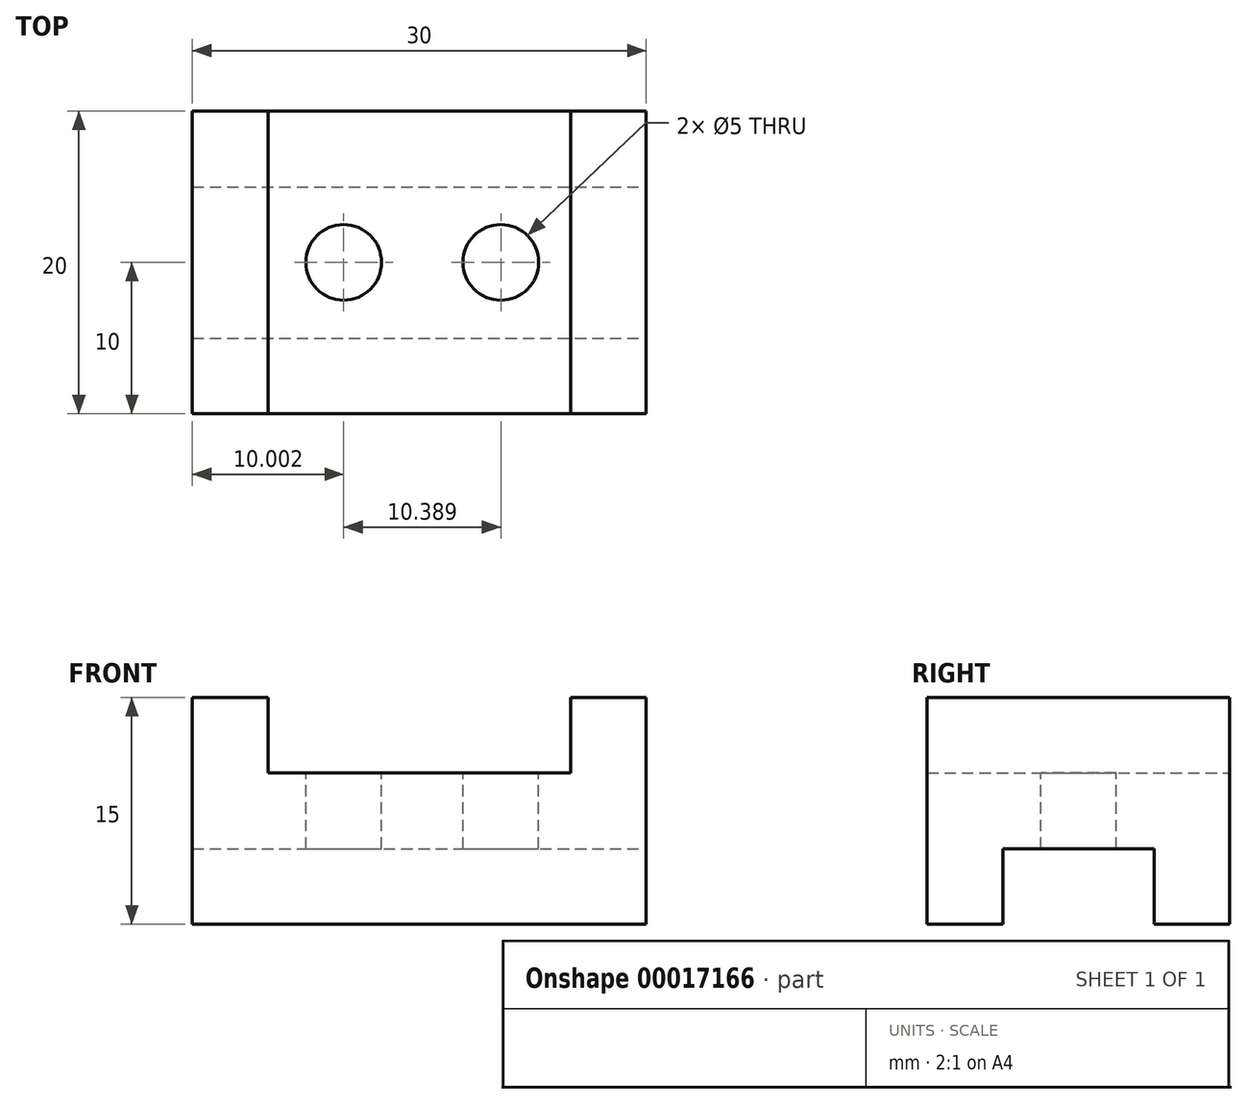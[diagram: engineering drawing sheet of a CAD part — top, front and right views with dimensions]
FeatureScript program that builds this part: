
annotation { "Feature Type Name" : "Feature", "Feature Type Description" : "" }
export const myFeature = defineFeature(function(context is Context, id is Id, definition is map)
    precondition{}
    {
        {
            var Q0;
            Q0=qCreatedBy(makeId("Front.planeOp"),FACE);
            var sketch = newSketch(context, id + "F0", { "sketchPlane" : qUnion([Q0])});
            skLineSegment(sketch, "E0", {"start": v(-25.78, 15) * mm, "end": v(-25.78, 0) * mm});
            skLineSegment(sketch, "E1", {"start": v(-25.78, 0) * mm, "end": v(4.22, 0) * mm});
            skLineSegment(sketch, "E2", {"start": v(4.22, 0) * mm, "end": v(4.22, 15) * mm});
            skLineSegment(sketch, "E3", {"start": v(4.22, 15) * mm, "end": v(-0.78, 15) * mm});
            skLineSegment(sketch, "E4", {"start": v(-0.78, 15) * mm, "end": v(-0.78, 10) * mm});
            skLineSegment(sketch, "E5", {"start": v(-0.78, 10) * mm, "end": v(-20.78, 10) * mm});
            skLineSegment(sketch, "E6", {"start": v(-25.78, 15) * mm, "end": v(-20.78, 15) * mm});
            skLineSegment(sketch, "E7", {"start": v(-20.78, 15) * mm, "end": v(-20.78, 10) * mm});
            skSolve(sketch);
        }
        {
            var Q0;
            Q0 = qSketchRegion(id + "F0", true);
            extrude(context, id + "F1", {"entities" : qUnion([Q0]), "depth" : 20 * mm});
        }
        {
            var Q0;
            Q0=makeQuery(id+"F1.opExtrude","SWEPT_FACE",FACE,{"disambiguationData":[OSD([sQuery(id+"F0.wireOp",EDGE,"E2")])]});
            var sketch = newSketch(context, id + "F2", { "sketchPlane" : qUnion([Q0])});
            skLineSegment(sketch, "E8", {"start": v(-15, 0) * mm, "end": v(-15, 5) * mm});
            skLineSegment(sketch, "E9", {"start": v(-15, 5) * mm, "end": v(-5, 5) * mm});
            skLineSegment(sketch, "E10", {"start": v(-5, 5) * mm, "end": v(-5, 0) * mm});
            skSolve(sketch);
        }
        {
            var Q0;
            Q0 = qSketchRegion(id + "F2", true);
            var Q1;
            {var subQ2=sQuery(id+"F2.wireOp",EDGE,"E8");Q1=makeQuery(id+"F2.imprint","IMPRINT",FACE,{"disambiguationData":[TD([[makeQuery(id+"F2.imprint","IMPRINT",EDGE,{"derivedFrom":subQ2}),-1.0]])]});}
            extrude(context, id + "F3", {"entities" : qUnion([Q0, Q1]), "operationType" : NewBodyOperationType.REMOVE, "endBound" : BoundingType.THROUGH_ALL, "oppositeDirection" : true, "depth" : 25 * mm});
        }
        {
            var Q0;
            Q0=makeQuery(id+"F1.opExtrude","SWEPT_FACE",FACE,{"disambiguationData":[OSD([sQuery(id+"F0.wireOp",EDGE,"E5")])]});
            var sketch = newSketch(context, id + "F4", { "sketchPlane" : qUnion([Q0])});
            skCircle(sketch, "E11", {"center": v(-15.78, -10) * mm, "radius": 2.5 * mm});
            skCircle(sketch, "E12", {"center": v(-5.39, -10) * mm, "radius": 2.5 * mm});
            skSolve(sketch);
        }
        {
            var Q0;
            Q0 = qSketchRegion(id + "F4", true);
            var Q1;
            Q1=makeQuery(id+"F4.imprint","IMPRINT",FACE,{"disambiguationData":[TD([[makeQuery(id+"F4.imprint","IMPRINT",EDGE,{"derivedFrom":sQuery(id+"F4.wireOp",EDGE,"E11")}),1.0]])]});
            extrude(context, id + "F5", {"entities" : qUnion([Q0, Q1]), "operationType" : NewBodyOperationType.REMOVE, "endBound" : BoundingType.THROUGH_ALL, "oppositeDirection" : true, "depth" : 25 * mm});
        }
    });
